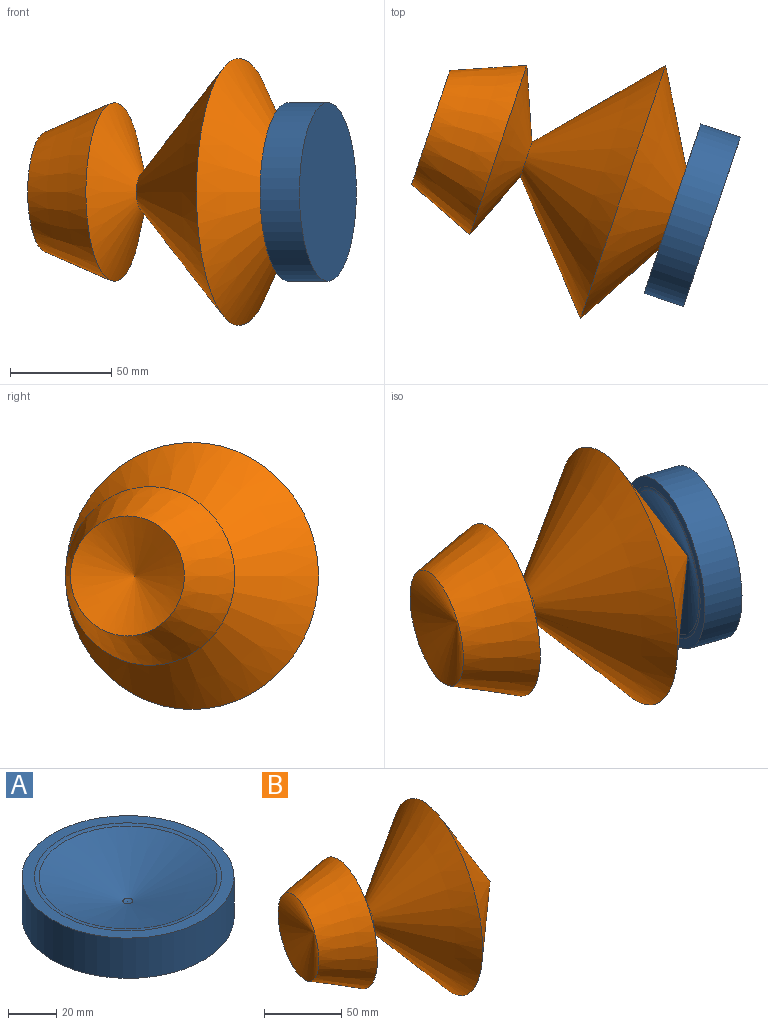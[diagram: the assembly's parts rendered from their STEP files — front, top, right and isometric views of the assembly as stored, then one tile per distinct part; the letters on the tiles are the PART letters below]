
ASSEMBLY  parts=2 mates=1
PART A: 6 faces, bbox 94.1x94.1x20.5 mm
  f0: sphere r=6.47mm, area 14.2mm2, adj f1
  f1: cone r=37.04mm half-angle=71.1deg, axis (0,0,1), area 4543.1mm2, adj f0,f2
  f2: torus R=38.98mm, axis (0,0,-1), area 469.6mm2, adj f1,f3
  f3: plane 88.3x88.3mm, normal (0,0,1), area 1350.4mm2, adj f2,f4
  f4: cylinder r=44.15mm len=88.3mm, axis (0,0,-1), area 5691.6mm2, adj f3,f5
  f5: plane 88.3x88.3mm, normal (0,0,-1), area 6124mm2, adj f4
PART B: 5 faces, bbox 140.6x125.1x132 mm
  f0: cone r=8.92mm half-angle=48.5deg, axis (0.95,-0.32,0), area 17933.9mm2, adj f1,f4
  f1: cone r=44.16mm half-angle=67.6deg, axis (-0.95,0.32,0), area 6353.6mm2, adj f0,f2
  f2: cone r=29.66mm half-angle=22.4deg, axis (0.95,-0.32,0), area 8835.7mm2, adj f1,f3
  f3: cone r=0mm half-angle=69.1deg, axis (-0.95,0.32,0), area 2958.5mm2, adj f2
  f4: cone r=65.99mm half-angle=60deg, axis (-0.95,0.32,0), area 15797.6mm2, adj f0
PLACE A rot(axis=(-0.16,-0.97,-0.16),91.5deg) t=(22.91,-77.31,0)mm
PLACE B at identity
MATE cylindrical A.f1 <-> B.f4  axis (-0.95,0.32,0) through (15.1,-74.69,0)mm
